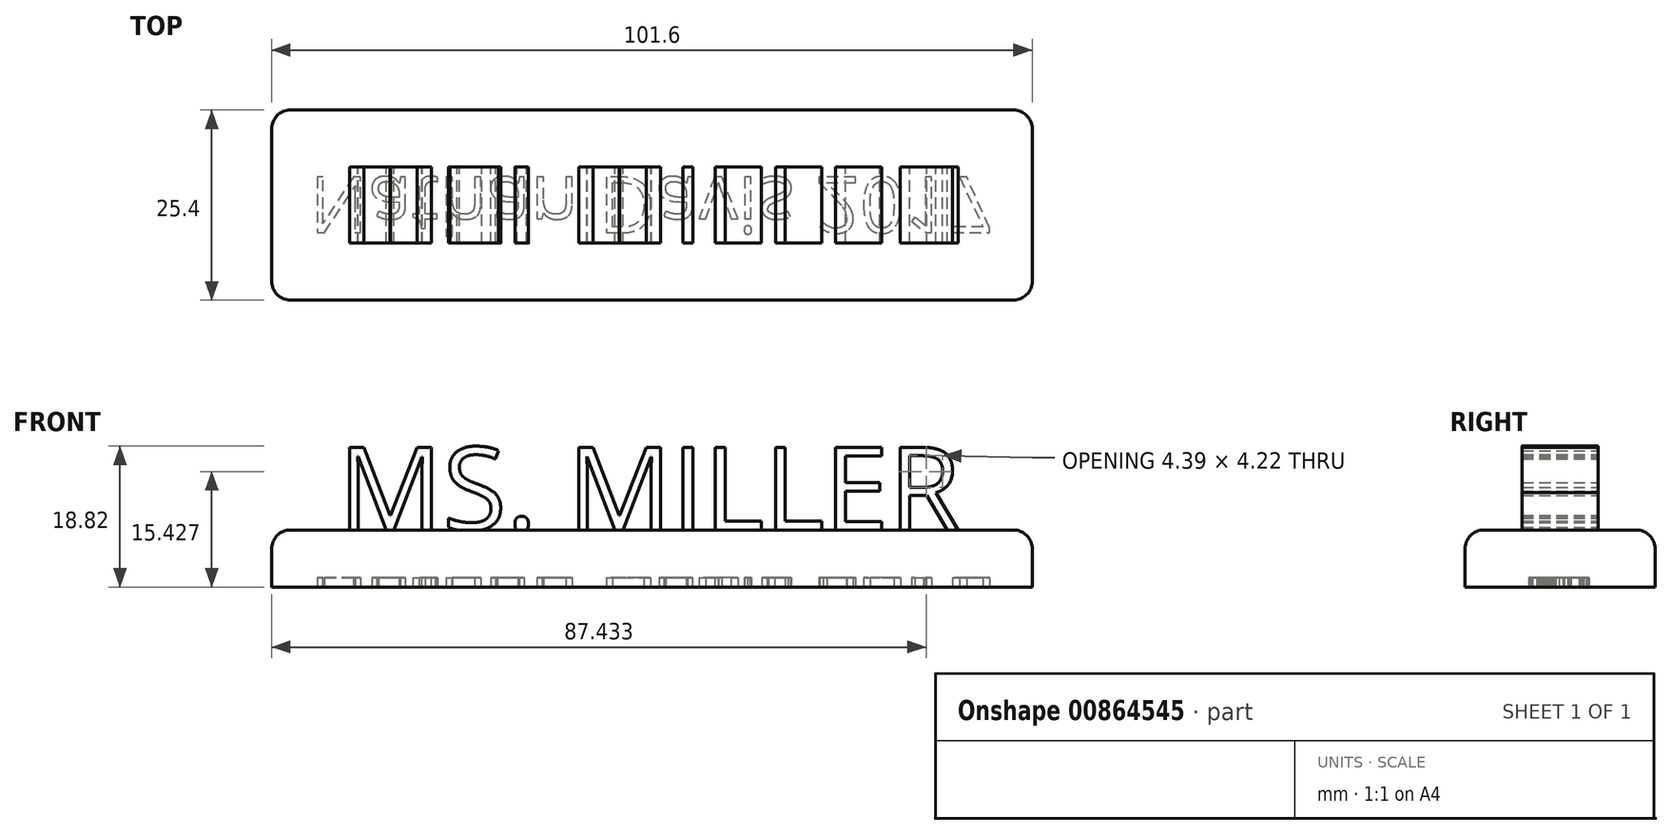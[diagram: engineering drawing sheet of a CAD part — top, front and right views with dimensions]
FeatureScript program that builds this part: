
annotation { "Feature Type Name" : "Feature", "Feature Type Description" : "" }
export const myFeature = defineFeature(function(context is Context, id is Id, definition is map)
    precondition{}
    {
        {
            var Q0;
            Q0=qCreatedBy(makeId("Top.planeOp"),FACE);
            var sketch = newSketch(context, id + "F0", { "sketchPlane" : qUnion([Q0])});
            skLineSegment(sketch, "E0.bottom", {"start": v(50.8, -12.7) * mm, "end": v(-50.8, -12.7) * mm});
            skLineSegment(sketch, "E0.top", {"start": v(50.8, 12.7) * mm, "end": v(-50.8, 12.7) * mm});
            skLineSegment(sketch, "E0.left", {"start": v(50.8, -12.7) * mm, "end": v(50.8, 12.7) * mm});
            skLineSegment(sketch, "E0.right", {"start": v(-50.8, -12.7) * mm, "end": v(-50.8, 12.7) * mm});
            skPoint(sketch, "E0.middle", {"position": v(0, 0) * mm});
            skSolve(sketch);
        }
        {
            var Q0;
            Q0 = qSketchRegion(id + "F0", true);
            extrude(context, id + "F1", {"entities" : qUnion([Q0]), "depth" : 7.62 * mm, "offsetDistance" : 25.4 * mm});
        }
        {
            var Q0;
            Q0=makeQuery(id+"F1.opExtrude","SWEPT_EDGE",EDGE,{"disambiguationData":[OSD([sQuery(id+"F0.wireOp",EDGE,"E0.top"),sQuery(id+"F0.wireOp",EDGE,"E0.right")])]});
            var Q1;
            Q1=makeQuery(id+"F1.opExtrude","SWEPT_EDGE",EDGE,{"disambiguationData":[OSD([sQuery(id+"F0.wireOp",EDGE,"E0.bottom"),sQuery(id+"F0.wireOp",EDGE,"E0.right")])]});
            var Q2;
            Q2=makeQuery(id+"F1.opExtrude","SWEPT_EDGE",EDGE,{"disambiguationData":[OSD([sQuery(id+"F0.wireOp",EDGE,"E0.bottom"),sQuery(id+"F0.wireOp",EDGE,"E0.left")])]});
            var Q3;
            Q3=makeQuery(id+"F1.opExtrude","SWEPT_EDGE",EDGE,{"disambiguationData":[OSD([sQuery(id+"F0.wireOp",EDGE,"E0.top"),sQuery(id+"F0.wireOp",EDGE,"E0.left")])]});
            var Q4;
            Q4=makeQuery(id+"F1.opExtrude","CAP_EDGE",EDGE,{"disambiguationData":[OSD([sQuery(id+"F0.wireOp",EDGE,"E0.bottom")])],"isStart":false});
            var Q5;
            Q5=makeQuery(id+"F1.opExtrude","CAP_EDGE",EDGE,{"disambiguationData":[OSD([sQuery(id+"F0.wireOp",EDGE,"E0.left")])],"isStart":false});
            var Q6;
            Q6=makeQuery(id+"F1.opExtrude","CAP_EDGE",EDGE,{"disambiguationData":[OSD([sQuery(id+"F0.wireOp",EDGE,"E0.top")])],"isStart":false});
            var Q7;
            Q7=makeQuery(id+"F1.opExtrude","CAP_EDGE",EDGE,{"disambiguationData":[OSD([sQuery(id+"F0.wireOp",EDGE,"E0.right")])],"isStart":false});
            fillet(context, id + "F2", {"entities" : qUnion([Q0, Q1, Q2, Q3, Q4, Q5, Q6, Q7]), "radius" : 2.54 * mm, "tangentPropagation" : true, "allowEdgeOverflow" : false});
        }
        {
            var Q0;
            Q0=qCreatedBy(makeId("Front.planeOp"),FACE);
            var sketch = newSketch(context, id + "F3", { "sketchPlane" : qUnion([Q0])});
            skText(sketch, "E1", { "text": "MS. MILLER", "fontName": "OpenSans-Regular.ttf"});
            const initialGuessF3  = {"E1": [-0.04191, 0.00762, 1, 0, 0.01114]};
            skSetInitialGuess(sketch, initialGuessF3);
            skSolve(sketch);
        }
        {
            var Q0;
            Q0 = qSketchRegion(id + "F3", true);
            extrude(context, id + "F4", {"entities" : qUnion([Q0]), "operationType" : NewBodyOperationType.ADD, "depth" : 5.08 * mm, "offsetDistance" : 25.4 * mm, "hasSecondDirection" : true, "secondDirectionOppositeDirection" : true, "secondDirectionDepth" : 5.08 * mm});
        }
        {
            var Q0;
            Q0=makeQuery(id+"F1.opExtrude","CAP_FACE",FACE,{"disambiguationData":[OSD([sQuery(id+"F0.wireOp",EDGE,"E0.bottom"),sQuery(id+"F0.wireOp",EDGE,"E0.top"),sQuery(id+"F0.wireOp",EDGE,"E0.left"),sQuery(id+"F0.wireOp",EDGE,"E0.right")])],"isStart":true});
            var sketch = newSketch(context, id + "F5", { "sketchPlane" : qUnion([Q0])});
            skText(sketch, "E2", { "text": "Nathan Davis 2017", "fontName": "OpenSans-Regular.ttf"});
            skLineSegment(sketch, "E3", {"start": v(45.72, 3.75) * mm, "end": v(45.72, 12.7) * mm, "construction": true});
            skLineSegment(sketch, "E4", {"start": v(45.72, -3.75) * mm, "end": v(45.72, -12.7) * mm, "construction": true});
            const initialGuessF5  = {"E2": [-0.04572, -0.00375, 1, 0, 0.0075]};
            skSetInitialGuess(sketch, initialGuessF5);
            skSolve(sketch);
        }
        {
            var Q0;
            Q0 = qSketchRegion(id + "F5", true);
            extrude(context, id + "F6", {"entities" : qUnion([Q0]), "operationType" : NewBodyOperationType.REMOVE, "oppositeDirection" : true, "depth" : 1.27 * mm, "offsetDistance" : 25.4 * mm});
        }
    });
